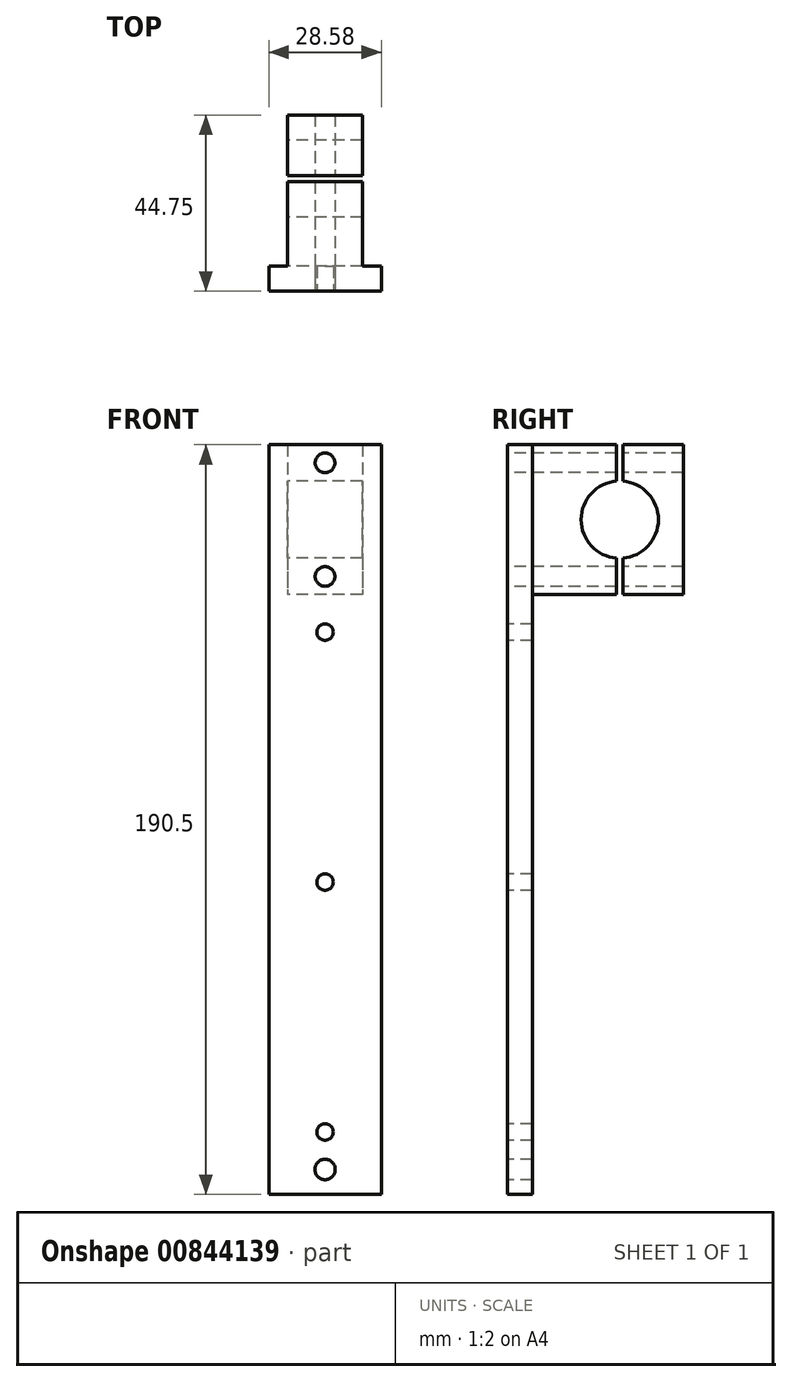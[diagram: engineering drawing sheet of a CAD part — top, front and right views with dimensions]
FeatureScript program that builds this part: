
annotation { "Feature Type Name" : "Feature", "Feature Type Description" : "" }
export const myFeature = defineFeature(function(context is Context, id is Id, definition is map)
    precondition{}
    {
        {
            var Q0;
            Q0=qCreatedBy(makeId("Right.planeOp"),FACE);
            var sketch = newSketch(context, id + "F0", { "sketchPlane" : qUnion([Q0])});
            skLineSegment(sketch, "E0.bottom", {"start": v(-28.58, 19.05) * mm, "end": v(-22.23, 19.05) * mm});
            skLineSegment(sketch, "E0.top", {"start": v(-28.57, -171.45) * mm, "end": v(-22.22, -171.45) * mm});
            skLineSegment(sketch, "E0.left", {"start": v(-28.58, 19.05) * mm, "end": v(-28.57, -171.45) * mm});
            skLineSegment(sketch, "E0.right", {"start": v(-22.23, 19.05) * mm, "end": v(-22.22, -171.45) * mm});
            skLineSegment(sketch, "E1.bottom", {"start": v(-22.23, 19.05) * mm, "end": v(-0.8, 19.05) * mm});
            skLineSegment(sketch, "E1.top", {"start": v(-22.23, -19.05) * mm, "end": v(-0.8, -19.05) * mm});
            skLineSegment(sketch, "E1.left", {"start": v(-22.23, 19.05) * mm, "end": v(-22.23, -19.05) * mm});
            skLineSegment(sketch, "E1.right", {"start": v(16.17, 19.05) * mm, "end": v(16.17, -19.05) * mm});
            skArc(sketch, "E2", {"start": v(-0.8, 9.78) * mm, "mid": v(-9.82, 0) * mm, "end": v(-0.8, -9.78) * mm});
            skLineSegment(sketch, "E3", {"start": v(16.17, 0) * mm, "end": v(0, 0) * mm, "construction": true});
            skLineSegment(sketch, "E4", {"start": v(-0.8, 19.05) * mm, "end": v(-0.8, 9.78) * mm});
            skLineSegment(sketch, "E5", {"start": v(0.8, 19.05) * mm, "end": v(0.8, 9.78) * mm});
            skLineSegment(sketch, "E6", {"start": v(0.8, 0) * mm, "end": v(-0.8, 0) * mm, "construction": true});
            skLineSegment(sketch, "E7.trimOffspring", {"start": v(0.8, 19.05) * mm, "end": v(16.17, 19.05) * mm});
            skArc(sketch, "E8.trimOffspring", {"start": v(0.8, -9.78) * mm, "mid": v(9.82, 0) * mm, "end": v(0.8, 9.78) * mm});
            skLineSegment(sketch, "E9.trimOffspring", {"start": v(0.8, -19.05) * mm, "end": v(16.17, -19.05) * mm});
            skLineSegment(sketch, "E10.trimOffspring", {"start": v(-0.8, -9.78) * mm, "end": v(-0.8, -19.05) * mm});
            skLineSegment(sketch, "E11.trimOffspring", {"start": v(0.8, -9.78) * mm, "end": v(0.8, -19.05) * mm});
            skSolve(sketch);
        }
        {
            var Q0;
            Q0=makeQuery(id+"F0.imprint","IMPRINT",FACE,{"disambiguationData":[TD([[makeQuery(id+"F0.imprint","IMPRINT",EDGE,{"derivedFrom":sQuery(id+"F0.wireOp",EDGE,"E0.bottom")}),-1.0]])]});
            extrude(context, id + "F1", {"entities" : qUnion([Q0]), "depth" : 14.29 * mm, "offsetDistance" : 25.4 * mm, "hasSecondDirection" : true, "secondDirectionOppositeDirection" : true, "secondDirectionDepth" : 14.29 * mm});
        }
        {
            var Q0;
            Q0=makeQuery(id+"F1.opExtrude","SWEPT_FACE",FACE,{"disambiguationData":[OSD([sQuery(id+"F0.wireOp",EDGE,"E0.left")])]});
            var sketch = newSketch(context, id + "F2", { "sketchPlane" : qUnion([Q0])});
            skCircle(sketch, "E12", {"center": v(0, -28.58) * mm, "radius": 2.1 * mm});
            skCircle(sketch, "E13", {"center": v(0, -92.08) * mm, "radius": 2.1 * mm});
            skCircle(sketch, "E14", {"center": v(0, -155.58) * mm, "radius": 2.1 * mm});
            skCircle(sketch, "E15", {"center": v(0, -165.1) * mm, "radius": 3 * mm});
            skCircle(sketch, "E16", {"center": v(0, 14.43) * mm, "radius": 2.5 * mm});
            skCircle(sketch, "E17", {"center": v(0, -14.43) * mm, "radius": 2.5 * mm});
            skLineSegment(sketch, "E18", {"start": v(0, 14.43) * mm, "end": v(0, 0) * mm, "construction": true});
            skLineSegment(sketch, "E19", {"start": v(0, 0) * mm, "end": v(0, -14.43) * mm, "construction": true});
            skSolve(sketch);
        }
        {
            var Q0;
            Q0=makeQuery(id+"F0.imprint","IMPRINT",FACE,{"disambiguationData":[TD([[makeQuery(id+"F0.imprint","IMPRINT",EDGE,{"derivedFrom":sQuery(id+"F0.wireOp",EDGE,"E1.bottom")}),-1.0]])]});
            var Q1;
            Q1=makeQuery(id+"F0.imprint","IMPRINT",FACE,{"disambiguationData":[TD([[makeQuery(id+"F0.imprint","IMPRINT",EDGE,{"derivedFrom":sQuery(id+"F0.wireOp",EDGE,"E1.right")}),-1.0]])]});
            extrude(context, id + "F3", {"entities" : qUnion([Q0, Q1]), "operationType" : NewBodyOperationType.ADD, "depth" : 9.52 * mm, "offsetDistance" : 25.4 * mm, "hasSecondDirection" : true, "secondDirectionOppositeDirection" : true, "secondDirectionDepth" : 9.52 * mm});
        }
        {
            var Q0;
            Q0=sQuery(id+"F2.wireOp",VERTEX,"E18.start");
            var Q1;
            Q1=sQuery(id+"F2.wireOp",VERTEX,"E19.end");
            var Q2;
            Q2=makeQuery(id+"F1.opExtrude","SWEPT_BODY",BODY,{"disambiguationData":[OSD([sQuery(id+"F0.wireOp",EDGE,"E0.bottom"),sQuery(id+"F0.wireOp",EDGE,"E0.top"),sQuery(id+"F0.wireOp",EDGE,"E0.left"),sQuery(id+"F0.wireOp",EDGE,"E0.right"),sQuery(id+"F0.wireOp",EDGE,"E1.left")])]});
            var Q3;
            Q3=makeQuery(id+"F3.opExtrude","SWEPT_BODY",BODY,{"disambiguationData":[OSD([sQuery(id+"F0.wireOp",EDGE,"E1.right"),sQuery(id+"F0.wireOp",EDGE,"E5"),sQuery(id+"F0.wireOp",EDGE,"E7.trimOffspring"),sQuery(id+"F0.wireOp",EDGE,"E8.trimOffspring"),sQuery(id+"F0.wireOp",EDGE,"E9.trimOffspring"),sQuery(id+"F0.wireOp",EDGE,"E11.trimOffspring")])]});
            hole(context, id + "F4", {"style" : HoleStyle.C_BORE, "endStyle" : HoleEndStyle.BLIND, "holeDiameter" : 5 * mm, "cBoreDiameter" : 11.25 * mm, "cBoreDepth" : 0 * mm, "majorDiameter" : 6.35 * mm, "holeDepth" : 76.2 * mm, "isTappedThrough" : true, "tappedDepth" : 12.7 * mm, "tapClearance" : 3, "locations" : qUnion([Q0, Q1]), "scope" : qUnion([Q2, Q3])});
        }
        {
            var Q0;
            Q0=sQuery(id+"F2.wireOp",VERTEX,"E12.center");
            var Q1;
            Q1=sQuery(id+"F2.wireOp",VERTEX,"E13.center");
            var Q2;
            Q2=sQuery(id+"F2.wireOp",VERTEX,"E14.center");
            var Q3;
            Q3=makeQuery(id+"F1.opExtrude","SWEPT_BODY",BODY,{"disambiguationData":[OSD([sQuery(id+"F0.wireOp",EDGE,"E0.bottom"),sQuery(id+"F0.wireOp",EDGE,"E0.top"),sQuery(id+"F0.wireOp",EDGE,"E0.left"),sQuery(id+"F0.wireOp",EDGE,"E0.right"),sQuery(id+"F0.wireOp",EDGE,"E1.left")])]});
            hole(context, id + "F5", {"style" : HoleStyle.C_BORE, "endStyle" : HoleEndStyle.BLIND, "holeDiameter" : 4.2 * mm, "cBoreDiameter" : 11.25 * mm, "cBoreDepth" : 0 * mm, "majorDiameter" : 6.35 * mm, "holeDepth" : 76.2 * mm, "isTappedThrough" : true, "tappedDepth" : 12.7 * mm, "tapClearance" : 3, "locations" : qUnion([Q0, Q1, Q2]), "scope" : qUnion([Q3])});
        }
        {
            var Q0;
            Q0=sQuery(id+"F2.wireOp",VERTEX,"E15.center");
            var Q1;
            Q1=makeQuery(id+"F1.opExtrude","SWEPT_BODY",BODY,{"disambiguationData":[OSD([sQuery(id+"F0.wireOp",EDGE,"E0.bottom"),sQuery(id+"F0.wireOp",EDGE,"E0.top"),sQuery(id+"F0.wireOp",EDGE,"E0.left"),sQuery(id+"F0.wireOp",EDGE,"E0.right"),sQuery(id+"F0.wireOp",EDGE,"E1.left")])]});
            hole(context, id + "F6", {"style" : HoleStyle.C_BORE, "endStyle" : HoleEndStyle.BLIND, "holeDiameter" : 5.18 * mm, "cBoreDiameter" : 11.25 * mm, "cBoreDepth" : 0 * mm, "majorDiameter" : 6.35 * mm, "holeDepth" : 76.2 * mm, "isTappedThrough" : true, "tappedDepth" : 12.7 * mm, "tapClearance" : 3, "locations" : qUnion([Q0]), "scope" : qUnion([Q1])});
        }
    });
